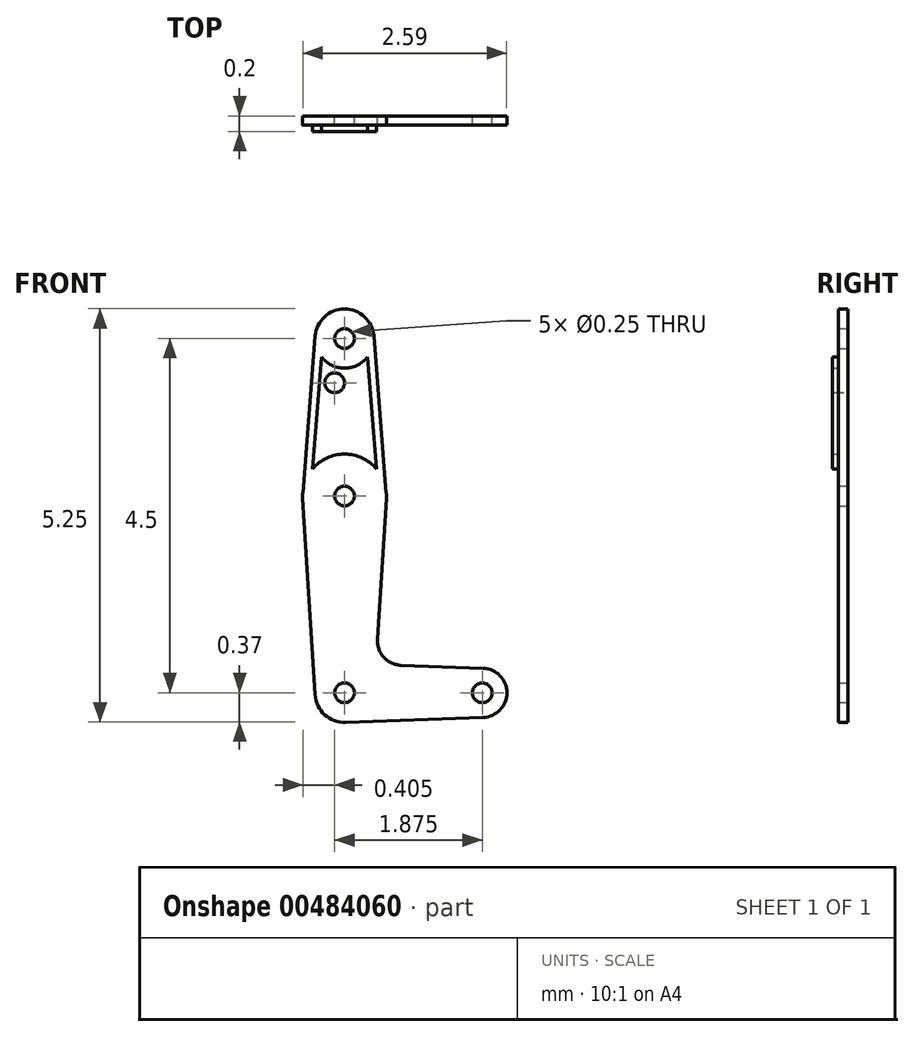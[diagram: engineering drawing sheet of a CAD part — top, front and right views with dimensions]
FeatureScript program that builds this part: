
annotation { "Feature Type Name" : "Feature", "Feature Type Description" : "" }
export const myFeature = defineFeature(function(context is Context, id is Id, definition is map)
    precondition{}
    {
        {
            var Q0;
            Q0=qCreatedBy(makeId("Front.planeOp"),FACE);
            var sketch = newSketch(context, id + "F0", { "sketchPlane" : qUnion([Q0])});
            skLineSegment(sketch, "E0", {"start": v(14.88, 6.88) * mm, "end": v(14.88, 2.38) * mm, "construction": true});
            skLineSegment(sketch, "E1", {"start": v(14.88, 2.38) * mm, "end": v(16.63, 2.38) * mm, "construction": true});
            skArc(sketch, "E2", {"start": v(14.59, 6.65) * mm, "mid": v(14.88, 6.5) * mm, "end": v(15.17, 6.65) * mm});
            skArc(sketch, "E3", {"start": v(14.35, 4.92) * mm, "mid": v(14.88, 4.35) * mm, "end": v(15.41, 4.92) * mm});
            skCircle(sketch, "E4", {"center": v(14.88, 2.38) * mm, "radius": 0.38 * mm});
            skCircle(sketch, "E5", {"center": v(16.63, 2.38) * mm, "radius": 0.31 * mm});
            skLineSegment(sketch, "E6", {"start": v(14.5, 6.9) * mm, "end": v(14.35, 4.92) * mm});
            skLineSegment(sketch, "E7", {"start": v(15.25, 6.9) * mm, "end": v(15.41, 4.92) * mm});
            skLineSegment(sketch, "E8", {"start": v(14.35, 4.85) * mm, "end": v(14.5, 2.36) * mm});
            skLineSegment(sketch, "E9", {"start": v(15.3, 3.06) * mm, "end": v(15.41, 4.85) * mm});
            skLineSegment(sketch, "E10", {"start": v(15.6, 2.73) * mm, "end": v(16.64, 2.7) * mm});
            skLineSegment(sketch, "E11", {"start": v(14.9, 2) * mm, "end": v(16.64, 2.07) * mm});
            skArc(sketch, "E12.filletArc", {"start": v(15.3, 3.06) * mm, "mid": v(15.38, 2.83) * mm, "end": v(15.6, 2.73) * mm});
            skCircle(sketch, "E13", {"center": v(14.88, 6.88) * mm, "radius": 0.12 * mm});
            skCircle(sketch, "E14", {"center": v(14.88, 4.88) * mm, "radius": 0.12 * mm});
            skCircle(sketch, "E15", {"center": v(14.88, 2.38) * mm, "radius": 0.12 * mm});
            skCircle(sketch, "E16", {"center": v(16.63, 2.38) * mm, "radius": 0.12 * mm});
            skCircle(sketch, "E17", {"center": v(14.76, 6.32) * mm, "radius": 0.12 * mm});
            skLineSegment(sketch, "E18", {"start": v(14.47, 5.22) * mm, "end": v(14.59, 6.65) * mm});
            skLineSegment(sketch, "E19", {"start": v(15.17, 6.65) * mm, "end": v(15.29, 5.22) * mm});
            skArc(sketch, "E20.trimOffspring", {"start": v(15.25, 6.9) * mm, "mid": v(14.88, 7.26) * mm, "end": v(14.5, 6.9) * mm});
            skArc(sketch, "E21.trimOffspring", {"start": v(15.29, 5.22) * mm, "mid": v(14.88, 5.41) * mm, "end": v(14.47, 5.22) * mm});
            skSolve(sketch);
        }
        {
            var Q0;
            Q0=makeQuery(id+"F0.imprint","IMPRINT",FACE,{"disambiguationData":[TD([[makeQuery(id+"F0.imprint","IMPRINT",EDGE,{"derivedFrom":sQuery(id+"F0.wireOp",EDGE,"E13")}),-1.0]])]});
            var Q1;
            {var subQ0=sQuery(id+"F0.wireOp",EDGE,"E6");Q1=makeQuery(id+"F0.imprint","IMPRINT",FACE,{"disambiguationData":[TD([[makeQuery(id+"F0.imprint","IMPRINT",EDGE,{"derivedFrom":subQ0}),1.0]])]});}
            var Q2;
            Q2=makeQuery(id+"F0.imprint","IMPRINT",FACE,{"disambiguationData":[TD([[makeQuery(id+"F0.imprint","IMPRINT",EDGE,{"derivedFrom":sQuery(id+"F0.wireOp",EDGE,"E14")}),-1.0]])]});
            var Q3;
            {var subQ3=sQuery(id+"F0.wireOp",EDGE,"E8");Q3=makeQuery(id+"F0.imprint","IMPRINT",FACE,{"disambiguationData":[TD([[makeQuery(id+"F0.imprint","IMPRINT",EDGE,{"derivedFrom":subQ3}),1.0]])]});}
            var Q4;
            Q4=makeQuery(id+"F0.imprint","IMPRINT",FACE,{"disambiguationData":[TD([[makeQuery(id+"F0.imprint","IMPRINT",EDGE,{"derivedFrom":sQuery(id+"F0.wireOp",EDGE,"E16")}),-1.0]])]});
            var Q5;
            Q5=makeQuery(id+"F0.imprint","IMPRINT",FACE,{"disambiguationData":[TD([[makeQuery(id+"F0.imprint","IMPRINT",EDGE,{"derivedFrom":sQuery(id+"F0.wireOp",EDGE,"E15")}),-1.0]])]});
            extrude(context, id + "F1", {"entities" : qUnion([Q0, Q1, Q2, Q3, Q4, Q5]), "depth" : .12 * mm});
        }
        {
            var Q0;
            Q0=makeQuery(id+"F0.imprint","IMPRINT",FACE,{"disambiguationData":[TD([[makeQuery(id+"F0.imprint","IMPRINT",EDGE,{"derivedFrom":sQuery(id+"F0.wireOp",EDGE,"E2")}),-1.0]])]});
            extrude(context, id + "F2", {"entities" : qUnion([Q0]), "operationType" : NewBodyOperationType.ADD, "depth" : .2 * mm});
        }
    });
